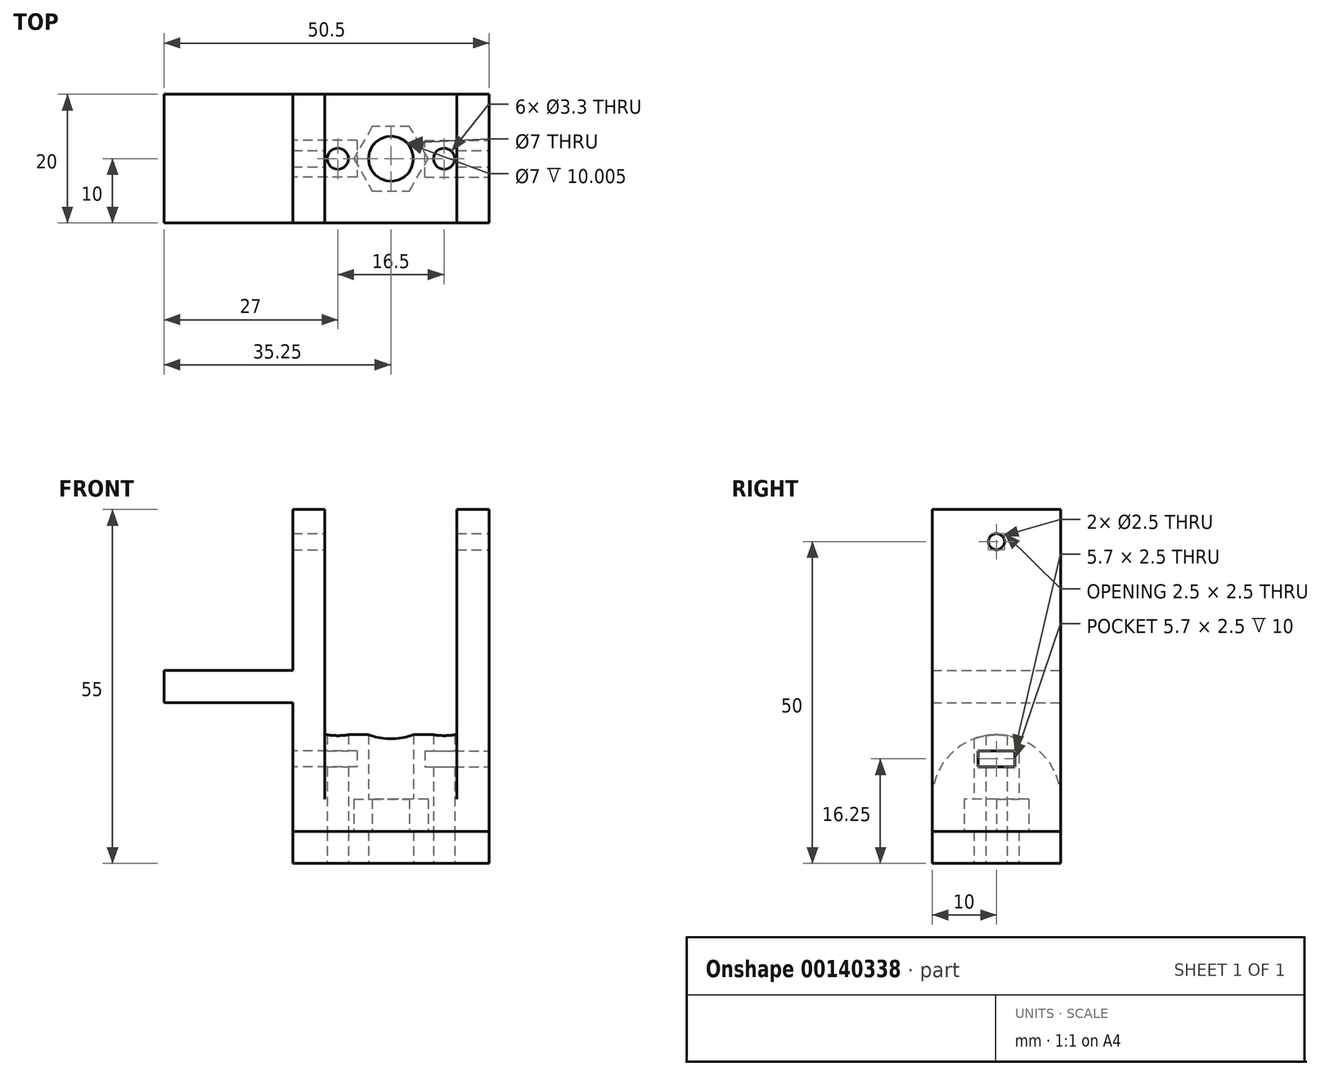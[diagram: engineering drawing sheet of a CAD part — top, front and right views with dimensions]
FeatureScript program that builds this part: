
annotation { "Feature Type Name" : "Feature", "Feature Type Description" : "" }
export const myFeature = defineFeature(function(context is Context, id is Id, definition is map)
    precondition{}
    {
        {
            var Q0;
            Q0=qCreatedBy(makeId("Front.planeOp"),FACE);
            var sketch = newSketch(context, id + "F0", { "sketchPlane" : qUnion([Q0])});
            skLineSegment(sketch, "E0", {"start": v(0, 0) * mm, "end": v(0, 5) * mm, "construction": true});
            skLineSegment(sketch, "E1", {"start": v(0, 5) * mm, "end": v(10.25, 5) * mm});
            skLineSegment(sketch, "E2", {"start": v(10.25, 5) * mm, "end": v(10.25, 50) * mm});
            skLineSegment(sketch, "E3", {"start": v(10.25, 50) * mm, "end": v(15.25, 50) * mm});
            skLineSegment(sketch, "E4", {"start": v(15.25, 50) * mm, "end": v(15.25, 0) * mm});
            skLineSegment(sketch, "E5", {"start": v(0, 0) * mm, "end": v(15.25, 0) * mm});
            skLineSegment(sketch, "E6.MirrorCS", {"start": v(0, 5) * mm, "end": v(-10.25, 5) * mm});
            skLineSegment(sketch, "E7.MirrorCS", {"start": v(-10.25, 5) * mm, "end": v(-10.25, 50) * mm});
            skLineSegment(sketch, "E8.MirrorCS", {"start": v(-10.25, 50) * mm, "end": v(-15.25, 50) * mm});
            skLineSegment(sketch, "E9.MirrorCS", {"start": v(-15.25, 50) * mm, "end": v(-15.25, 25) * mm});
            skLineSegment(sketch, "E10.MirrorCS", {"start": v(0, 0) * mm, "end": v(-15.25, 0) * mm});
            skLineSegment(sketch, "E11", {"start": v(-15.25, 20) * mm, "end": v(-35.25, 20) * mm});
            skLineSegment(sketch, "E12", {"start": v(-35.25, 20) * mm, "end": v(-35.25, 25) * mm});
            skLineSegment(sketch, "E13", {"start": v(-35.25, 25) * mm, "end": v(-15.25, 25) * mm});
            skLineSegment(sketch, "E14.trimOffspring", {"start": v(-15.25, 20) * mm, "end": v(-15.25, 0) * mm});
            skSolve(sketch);
        }
        {
            var Q0;
            Q0 = qSketchRegion(id + "F0", true);
            extrude(context, id + "F1", {"entities" : qUnion([Q0]), "endBound" : BoundingType.SYMMETRIC, "depth" : 20 * mm, "hasSecondDirection" : true, "secondDirectionOppositeDirection" : true, "secondDirectionDepth" : 25 * mm});
        }
        {
            var Q0;
            Q0=makeQuery(id+"F1.opExtrude","SWEPT_FACE",FACE,{"disambiguationData":[OSD([sQuery(id+"F0.wireOp",EDGE,"E5"),sQuery(id+"F0.wireOp",EDGE,"E10.MirrorCS")])]});
            var sketch = newSketch(context, id + "F2", { "sketchPlane" : qUnion([Q0])});
            skCircle(sketch, "E15.cCircle", {"center": v(0, 0) * mm, "radius": 5 * mm, "construction": true});
            skLineSegment(sketch, "E15.0", {"start": v(-2.89, 5) * mm, "end": v(2.89, 5) * mm});
            skLineSegment(sketch, "E15.1", {"start": v(2.89, 5) * mm, "end": v(5.77, 0) * mm});
            skLineSegment(sketch, "E15.2", {"start": v(5.77, 0) * mm, "end": v(2.89, -5) * mm});
            skLineSegment(sketch, "E15.3", {"start": v(2.89, -5) * mm, "end": v(-2.89, -5) * mm});
            skLineSegment(sketch, "E15.4", {"start": v(-2.89, -5) * mm, "end": v(-5.77, 0) * mm});
            skLineSegment(sketch, "E15.5", {"start": v(-5.77, 0) * mm, "end": v(-2.89, 5) * mm});
            skPoint(sketch, "E15.0.midPoint", {"position": v(0, 5) * mm});
            skPoint(sketch, "E16.centerSnap0", {"position": v(-15.25, 0) * mm});
            skSolve(sketch);
        }
        {
            var Q0;
            Q0=makeQuery(id+"F1.opExtrude","SWEPT_FACE",FACE,{"disambiguationData":[OSD([sQuery(id+"F0.wireOp",EDGE,"E5"),sQuery(id+"F0.wireOp",EDGE,"E10.MirrorCS")])]});
            var sketch = newSketch(context, id + "F3", { "sketchPlane" : qUnion([Q0])});
            skLineSegment(sketch, "E17.0", {"start": v(15.25, 10) * mm, "end": v(-15.25, 10) * mm});
            skLineSegment(sketch, "E18.0", {"start": v(-15.25, 10) * mm, "end": v(-15.25, -10) * mm});
            skLineSegment(sketch, "E19.0", {"start": v(15.25, -10) * mm, "end": v(-15.25, -10) * mm});
            skLineSegment(sketch, "E20.0", {"start": v(15.25, 10) * mm, "end": v(15.25, -10) * mm});
            skSolve(sketch);
        }
        {
            var Q0;
            Q0 = qSketchRegion(id + "F3", true);
            extrude(context, id + "F4", {"entities" : qUnion([Q0]), "depth" : 5 * mm});
        }
        {
            var Q0;
            Q0 = qSketchRegion(id + "F2", true);
            extrude(context, id + "F5", {"entities" : qUnion([Q0]), "operationType" : NewBodyOperationType.REMOVE, "oppositeDirection" : true, "depth" : 5 * mm});
        }
        {
            var Q0;
            Q0=makeQuery(id+"F4.opExtrude","CAP_FACE",FACE,{"disambiguationData":[OSD([sQuery(id+"F3.wireOp",EDGE,"E17.0"),sQuery(id+"F3.wireOp",EDGE,"E18.0"),sQuery(id+"F3.wireOp",EDGE,"E19.0"),sQuery(id+"F3.wireOp",EDGE,"E20.0")])],"isStart":false});
            var sketch = newSketch(context, id + "F6", { "sketchPlane" : qUnion([Q0])});
            skCircle(sketch, "E21", {"center": v(0, 0) * mm, "radius": 3.5 * mm});
            skCircle(sketch, "E22", {"center": v(-8.25, 0) * mm, "radius": 1.65 * mm});
            skCircle(sketch, "E23.MirrorC", {"center": v(8.25, 0) * mm, "radius": 1.65 * mm});
            skSolve(sketch);
        }
        {
            var Q0;
            Q0=makeQuery(id+"F1.opExtrude","SWEPT_FACE",FACE,{"disambiguationData":[OSD([sQuery(id+"F0.wireOp",EDGE,"E9.MirrorCS")])]});
            var sketch = newSketch(context, id + "F7", { "sketchPlane" : qUnion([Q0])});
            skLineSegment(sketch, "E24.bottom", {"start": v(-2.85, 12.5) * mm, "end": v(2.85, 12.5) * mm});
            skLineSegment(sketch, "E24.top", {"start": v(-2.85, 10) * mm, "end": v(2.85, 10) * mm});
            skLineSegment(sketch, "E24.left", {"start": v(-2.85, 12.5) * mm, "end": v(-2.85, 10) * mm});
            skLineSegment(sketch, "E24.right", {"start": v(2.85, 12.5) * mm, "end": v(2.85, 10) * mm});
            skLineSegment(sketch, "E25", {"start": v(0, 0) * mm, "end": v(0, 10) * mm, "construction": true});
            skSolve(sketch);
        }
        {
            var Q0;
            Q0=makeQuery(id+"F1.opExtrude","SWEPT_FACE",FACE,{"disambiguationData":[OSD([sQuery(id+"F0.wireOp",EDGE,"E4")])]});
            var sketch = newSketch(context, id + "F8", { "sketchPlane" : qUnion([Q0])});
            skLineSegment(sketch, "E26.bottom", {"start": v(-2.85, 12.5) * mm, "end": v(2.85, 12.5) * mm});
            skLineSegment(sketch, "E26.top", {"start": v(-2.85, 10) * mm, "end": v(2.85, 10) * mm});
            skLineSegment(sketch, "E26.left", {"start": v(-2.85, 12.5) * mm, "end": v(-2.85, 10) * mm});
            skLineSegment(sketch, "E26.right", {"start": v(2.85, 12.5) * mm, "end": v(2.85, 10) * mm});
            skLineSegment(sketch, "E27", {"start": v(0, 0) * mm, "end": v(0, 10) * mm, "construction": true});
            skSolve(sketch);
        }
        {
            var Q0;
            Q0=makeQuery(id+"F1.opExtrude","SWEPT_FACE",FACE,{"disambiguationData":[OSD([sQuery(id+"F0.wireOp",EDGE,"E7.MirrorCS")])]});
            var sketch = newSketch(context, id + "F9", { "sketchPlane" : qUnion([Q0])});
            skLineSegment(sketch, "E28", {"start": v(10, 5) * mm, "end": v(-10, 5) * mm});
            skArc(sketch, "E29", {"start": v(10, 5) * mm, "mid": v(0, 15) * mm, "end": v(-10, 5) * mm});
            skSolve(sketch);
        }
        {
            var Q0;
            Q0 = qSketchRegion(id + "F9", true);
            var Q1;
            Q1=makeQuery(id+"F1.opExtrude","SWEPT_FACE",FACE,{"disambiguationData":[OSD([sQuery(id+"F0.wireOp",EDGE,"E2")])]});
            extrude(context, id + "F10", {"entities" : qUnion([Q0]), "operationType" : NewBodyOperationType.ADD, "endBound" : BoundingType.UP_TO_SURFACE, "endBoundEntityFace" : qUnion([Q1]), "depth" : 25 * mm});
        }
        {
            var Q0;
            Q0 = qSketchRegion(id + "F6", true);
            extrude(context, id + "F11", {"entities" : qUnion([Q0]), "operationType" : NewBodyOperationType.REMOVE, "endBound" : BoundingType.THROUGH_ALL, "oppositeDirection" : true, "depth" : 25 * mm});
        }
        {
            var Q0;
            Q0=makeQuery(id+"F1.opExtrude","SWEPT_FACE",FACE,{"disambiguationData":[OSD([sQuery(id+"F0.wireOp",EDGE,"E4")])]});
            var sketch = newSketch(context, id + "F12", { "sketchPlane" : qUnion([Q0])});
            skCircle(sketch, "E30", {"center": v(0, 45) * mm, "radius": 1.25 * mm});
            skPoint(sketch, "E30.centerSnap0", {"position": v(0, 50) * mm});
            skSolve(sketch);
        }
        {
            var Q0;
            Q0 = qSketchRegion(id + "F12", true);
            extrude(context, id + "F13", {"entities" : qUnion([Q0]), "operationType" : NewBodyOperationType.REMOVE, "endBound" : BoundingType.THROUGH_ALL, "oppositeDirection" : true, "depth" : 25 * mm});
        }
        {
            var Q0;
            Q0 = qSketchRegion(id + "F7", true);
            extrude(context, id + "F14", {"entities" : qUnion([Q0]), "operationType" : NewBodyOperationType.REMOVE, "oppositeDirection" : true, "depth" : 10 * mm});
        }
        {
            var Q0;
            Q0 = qSketchRegion(id + "F8", true);
            extrude(context, id + "F15", {"entities" : qUnion([Q0]), "operationType" : NewBodyOperationType.REMOVE, "oppositeDirection" : true, "depth" : 10 * mm});
        }
    });
